# Revit family: SM52T-B
name_source: partatom
category: Communication Devices
revit_build: Autodesk Revit 2014 (Build: 20140709_2115(x64)
units: mm (PartAtom-declared; Revit-internal decimal feet)

## types (1)
- Surface Mount Loundspeaker
    100V Taps = .94, 1.9, 3.7, 7.5, 15, 30 & 8Ω bypass
    70V Taps = .94, 1.9, 3.7, 7.5, 15, 30 & 8Ω bypass
    Baffle Material = <By Category>
    Body Material = QF_Plastic - Black - Fine Textured
    Color = <By Category>
    Cost = 201.99 $
    Cost MSRP = 201.99 $
    Coverage Horizontal = 110.00°
    Coverage Vertical = 110.00°
    Depth = 11.57 "
    Description = 5.25" 2-WAY ALL WEATHER LOUDSPEAKER WITH 30-WATT 70V/100V TRANSFORMER - BLACK
    Dispersion Angle = 0.00°
    Enclosure Material = <By Category>
    Environmental Testing = 100HR Salt Spray Test Per ASTM B117
    Family Code (default) = LOUD SPEAKERS
    Frequency Response  = 85Hz – 20kHz (±3dB)
    Grill Material = QF_Plastic - Black - Fine Textured
    Height = 6.91 "
    IQ Category = SPEAKERS
    Impedance = 8
    Ingress Protection = IP-33
    Manufacturer = ATLAS SOUND
    Manufacturer URL = https://www.atlasied.com
    MasterFormat = 27 41 13
    MaterFormat Title = SPEAKERS
    Model = SM52T-B
    Mount Material = QF_Plastic - Black - Fine Textured
    OmniClass Number = 23-37 17 13 19
    OmniClass Title = SPEAKERS
    Pitch = 0.00°
    Power Rating (RMS) = 100 Watts
    Product Documentation Link = https://www.atlasied.com
    Product Page URL = https://www.atlasied.com
    Rotation = 0.00°
    SPL Max = 107
    ScheduleType |RF| = AtlasIED Master
    Sensitivity = 90
    Speaker Dispersion = 90.00°
    Transformer Option = Yes
    URL = www.atlassound.com
    Vertical Symmetry = Yes
    Warranty = 5 Year
    Weight Product = 7.5
    Width = 6.9 "

## geometry (parser evidence)
native form markers: Blend x10, Sweep x3
no freeform markers — native parametric forms only
